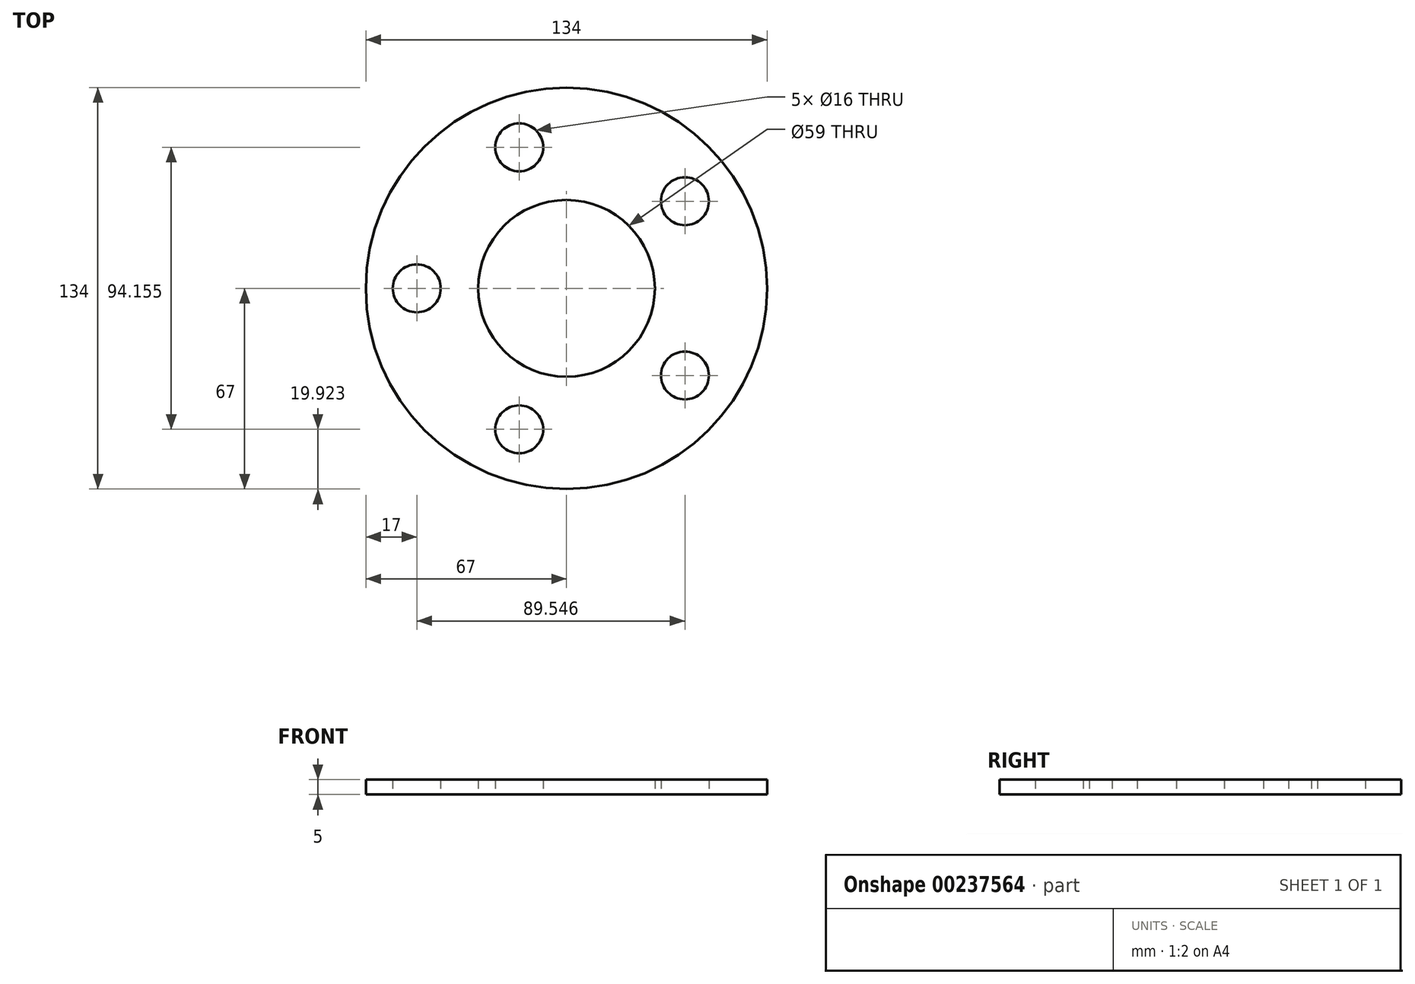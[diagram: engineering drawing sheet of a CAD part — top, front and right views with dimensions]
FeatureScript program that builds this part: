
annotation { "Feature Type Name" : "Feature", "Feature Type Description" : "" }
export const myFeature = defineFeature(function(context is Context, id is Id, definition is map)
    precondition{}
    {
        {
            var Q0;
            Q0=qCreatedBy(makeId("Top.planeOp"),FACE);
            var sketch = newSketch(context, id + "F0", { "sketchPlane" : qUnion([Q0])});
            skCircle(sketch, "E0", {"center": v(0, 0) * mm, "radius": 29.5 * mm});
            skCircle(sketch, "E1", {"center": v(-50, 0) * mm, "radius": 8 * mm});
            skCircle(sketch, "E2", {"center": v(0, 0) * mm, "radius": 50 * mm, "construction": true});
            skCircle(sketch, "E3.1.0", {"center": v(-15.8, 47.08) * mm, "radius": 8 * mm});
            skCircle(sketch, "E3.2.0", {"center": v(39.55, 29.1) * mm, "radius": 8 * mm});
            skCircle(sketch, "E3.3.0", {"center": v(39.55, -29.1) * mm, "radius": 8 * mm});
            skCircle(sketch, "E3.4.0", {"center": v(-15.8, -47.08) * mm, "radius": 8 * mm});
            skPoint(sketch, "E3.center", {"position": v(-0.5, 0) * mm});
            skLineSegment(sketch, "E3.anchor1", {"start": v(-0.5, 0) * mm, "end": v(-50, 0) * mm, "construction": true});
            skLineSegment(sketch, "E3.anchor2", {"start": v(-0.5, 0) * mm, "end": v(-15.8, -47.08) * mm, "construction": true});
            skCircle(sketch, "E4", {"center": v(0, 0) * mm, "radius": 67 * mm});
            skSolve(sketch);
        }
        {
            var Q0;
            Q0 = qSketchRegion(id + "F0", true);
            extrude(context, id + "F1", {"entities" : qUnion([Q0]), "depth" : 5 * mm});
        }
    });
